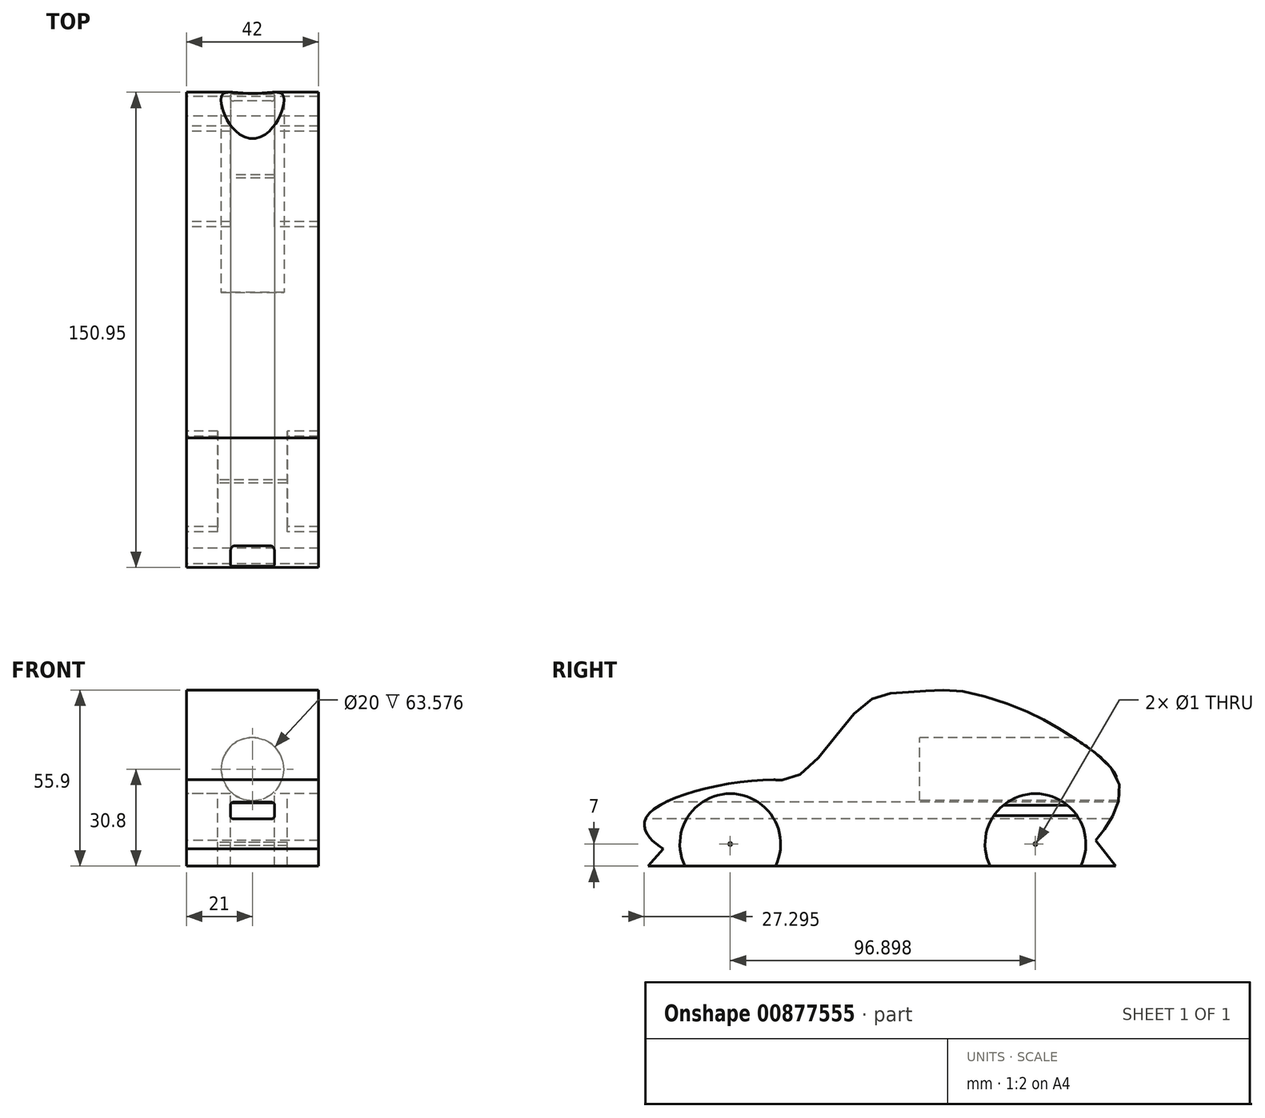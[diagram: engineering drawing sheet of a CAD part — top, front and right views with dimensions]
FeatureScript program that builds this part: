
annotation { "Feature Type Name" : "Feature", "Feature Type Description" : "" }
export const myFeature = defineFeature(function(context is Context, id is Id, definition is map)
    precondition{}
    {
        {
            var Q0;
            Q0=qCreatedBy(makeId("Right.planeOp"),FACE);
            var sketch = newSketch(context, id + "F0", { "sketchPlane" : qUnion([Q0])});
            skArc(sketch, "E0", {"start": v(63.2, 0) * mm, "mid": v(48.81, 23) * mm, "end": v(34.43, 0) * mm});
            skCircle(sketch, "E1", {"center": v(48.81, 7) * mm, "radius": 0.5 * mm});
            skLineSegment(sketch, "E2", {"start": v(-74.19, 0) * mm, "end": v(-69.32, 5.42) * mm});
            skLineSegment(sketch, "E3", {"start": v(74.24, 0) * mm, "end": v(68, 8.2) * mm});
            skLineSegment(sketch, "E4", {"start": v(34.43, 0) * mm, "end": v(63.2, 0) * mm});
            skLineSegment(sketch, "E5", {"start": v(63.2, 0) * mm, "end": v(74.24, 0) * mm});
            skFitSpline(sketch, "E6", {"points": [v(-69.32, 5.42) * mm, v(-74.16, 9.7) * mm, v(-74.86, 15.33) * mm, v(-52.68, 25.37) * mm, v(-23.1, 24.85) * mm], "startDerivative": vector(-34.94, 24.78) * mm, "endDerivative": vector(31.68, -31.68) * mm});
            skFitSpline(sketch, "E7", {"points": [v(68, 8.2) * mm, v(73.36, 16.04) * mm, v(74.77, 28) * mm, v(59.1, 41.91) * mm, v(46.07, 49.13) * mm, v(24.42, 55.65) * mm, v(9.81, 55.3) * mm, v(-5.33, 51.6) * mm, v(-26.85, 28.6) * mm, v(-34.3, 27.45) * mm, v(-34.27, 27.45) * mm], "startDerivative": vector(66.23, 83.04) * mm, "endDerivative": vector(8.76, -0.08) * mm});
            skArc(sketch, "E8", {"start": v(-33.7, 0) * mm, "mid": v(-48.09, 23) * mm, "end": v(-62.47, 0) * mm});
            skLineSegment(sketch, "E9", {"start": v(-74.19, 0) * mm, "end": v(-62.47, 0) * mm});
            skLineSegment(sketch, "E10", {"start": v(-62.47, 0) * mm, "end": v(-33.7, 0) * mm});
            skLineSegment(sketch, "E11", {"start": v(-33.7, 0) * mm, "end": v(34.43, 0) * mm});
            skCircle(sketch, "E12", {"center": v(-48.09, 7) * mm, "radius": 0.5 * mm});
            skSolve(sketch);
        }
        {
            var Q0;
            Q0=makeQuery(id+"F0.imprint","IMPRINT",FACE,{"disambiguationData":[TD([[makeQuery(id+"F0.imprint","IMPRINT",EDGE,{"derivedFrom":sQuery(id+"F0.wireOp",EDGE,"E0")}),-1.0]])]});
            extrude(context, id + "F1", {"entities" : qUnion([Q0]), "depth" : 21 * mm, "offsetDistance" : 25 * mm, "hasSecondDirection" : true, "secondDirectionOppositeDirection" : true, "secondDirectionDepth" : 21 * mm});
        }
        {
            var Q0;
            Q0=makeQuery(id+"F0.imprint","IMPRINT",FACE,{"disambiguationData":[TD([[makeQuery(id+"F0.imprint","IMPRINT",EDGE,{"derivedFrom":sQuery(id+"F0.wireOp",EDGE,"E8")}),1.0]])]});
            extrude(context, id + "F2", {"entities" : qUnion([Q0]), "operationType" : NewBodyOperationType.ADD, "depth" : 11 * mm, "offsetDistance" : 25 * mm, "hasSecondDirection" : true, "secondDirectionOppositeDirection" : true, "secondDirectionDepth" : 11 * mm});
        }
        {
            var Q0;
            Q0=makeQuery(id+"F0.imprint","IMPRINT",FACE,{"disambiguationData":[TD([[makeQuery(id+"F0.imprint","IMPRINT",EDGE,{"derivedFrom":sQuery(id+"F0.wireOp",EDGE,"E0")}),1.0]])]});
            extrude(context, id + "F3", {"entities" : qUnion([Q0]), "operationType" : NewBodyOperationType.ADD, "depth" : 7 * mm, "offsetDistance" : 25 * mm, "hasSecondDirection" : true, "secondDirectionOppositeDirection" : true, "secondDirectionDepth" : 7 * mm});
        }
        {
            var Q0;
            Q0=qCreatedBy(makeId("Front.planeOp"),FACE);
            var sketch = newSketch(context, id + "F4", { "sketchPlane" : qUnion([Q0])});
            skCircle(sketch, "E13", {"center": v(0, 30.8) * mm, "radius": 10 * mm});
            skSolve(sketch);
        }
        {
            var Q0;
            Q0 = qSketchRegion(id + "F4", true);
            extrude(context, id + "F5", {"entities" : qUnion([Q0]), "operationType" : NewBodyOperationType.REMOVE, "oppositeDirection" : true, "depth" : 76 * mm, "offsetDistance" : 25 * mm});
        }
        {
            var Q0;
            Q0 = qSketchRegion(id + "F4", true);
            extrude(context, id + "F6", {"entities" : qUnion([Q0]), "operationType" : NewBodyOperationType.ADD, "oppositeDirection" : true, "depth" : 12 * mm, "offsetDistance" : 25 * mm});
        }
        {
            var Q0;
            Q0=qCreatedBy(makeId("Front.planeOp"),FACE);
            var sketch = newSketch(context, id + "F7", { "sketchPlane" : qUnion([Q0])});
            skLineSegment(sketch, "E14.bottom", {"start": v(-6, 20.31) * mm, "end": v(6, 20.31) * mm});
            skLineSegment(sketch, "E14.top", {"start": v(-6, 15) * mm, "end": v(6, 15) * mm});
            skLineSegment(sketch, "E14.left", {"start": v(-7, 19.31) * mm, "end": v(-7, 16) * mm});
            skLineSegment(sketch, "E14.right", {"start": v(7, 19.31) * mm, "end": v(7, 16) * mm});
            skPoint(sketch, "E15.visualSharp", {"position": v(-7, 20.31) * mm});
            skArc(sketch, "E15.filletArc", {"start": v(-6, 20.31) * mm, "mid": v(-6.7, 20.02) * mm, "end": v(-7, 19.31) * mm});
            skPoint(sketch, "E16.visualSharp", {"position": v(7, 20.31) * mm});
            skArc(sketch, "E16.filletArc", {"start": v(7, 19.31) * mm, "mid": v(6.7, 20.02) * mm, "end": v(6, 20.31) * mm});
            skPoint(sketch, "E17.visualSharp", {"position": v(7, 15) * mm});
            skArc(sketch, "E17.filletArc", {"start": v(6, 15) * mm, "mid": v(6.7, 15.3) * mm, "end": v(7, 16) * mm});
            skPoint(sketch, "E18.visualSharp", {"position": v(-7, 15) * mm});
            skArc(sketch, "E18.filletArc", {"start": v(-7, 16) * mm, "mid": v(-6.7, 15.3) * mm, "end": v(-6, 15) * mm});
            skSolve(sketch);
        }
        {
            var Q0;
            Q0 = qSketchRegion(id + "F7", true);
            extrude(context, id + "F8", {"entities" : qUnion([Q0]), "operationType" : NewBodyOperationType.REMOVE, "oppositeDirection" : true, "depth" : 75 * mm, "offsetDistance" : 25 * mm, "hasSecondDirection" : true, "secondDirectionOppositeDirection" : false, "secondDirectionDepth" : 75 * mm});
        }
    });
